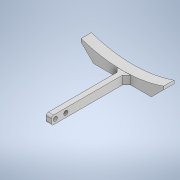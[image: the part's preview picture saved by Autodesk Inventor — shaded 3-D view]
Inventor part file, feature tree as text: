
AUTODESK INVENTOR PART (.ipt)
format: ipt  version: 2020 (Build 240168000, 168)  size: 177,152 bytes
history: native  units: mm
features: extrude x3, sketch x3, chamfer x2, fillet x1
ambient origin geometry x8: Origin, YZ Plane, XZ Plane, XY Plane, X Axis, Y Axis, Z Axis, Center Point
bodies: Solide1 (feature_tree)
feature tree (9):
  extrude  "Extrusion1"  Depth=15.0mm
  extrude  "Extrusion2"  Depth=80.0mm
  extrude  "Extrusion8"  Depth=10.0mm TaperAngle=0.0deg
  chamfer  "Chanfrein1"  Distance=5.0mm
  chamfer  "Chanfrein2"  Distance=80.0mm
  fillet  "Congé1"  Radius=72.9mm
  sketch  "Esquisse1"
  sketch  "Esquisse2"
  sketch  "Esquisse8"
